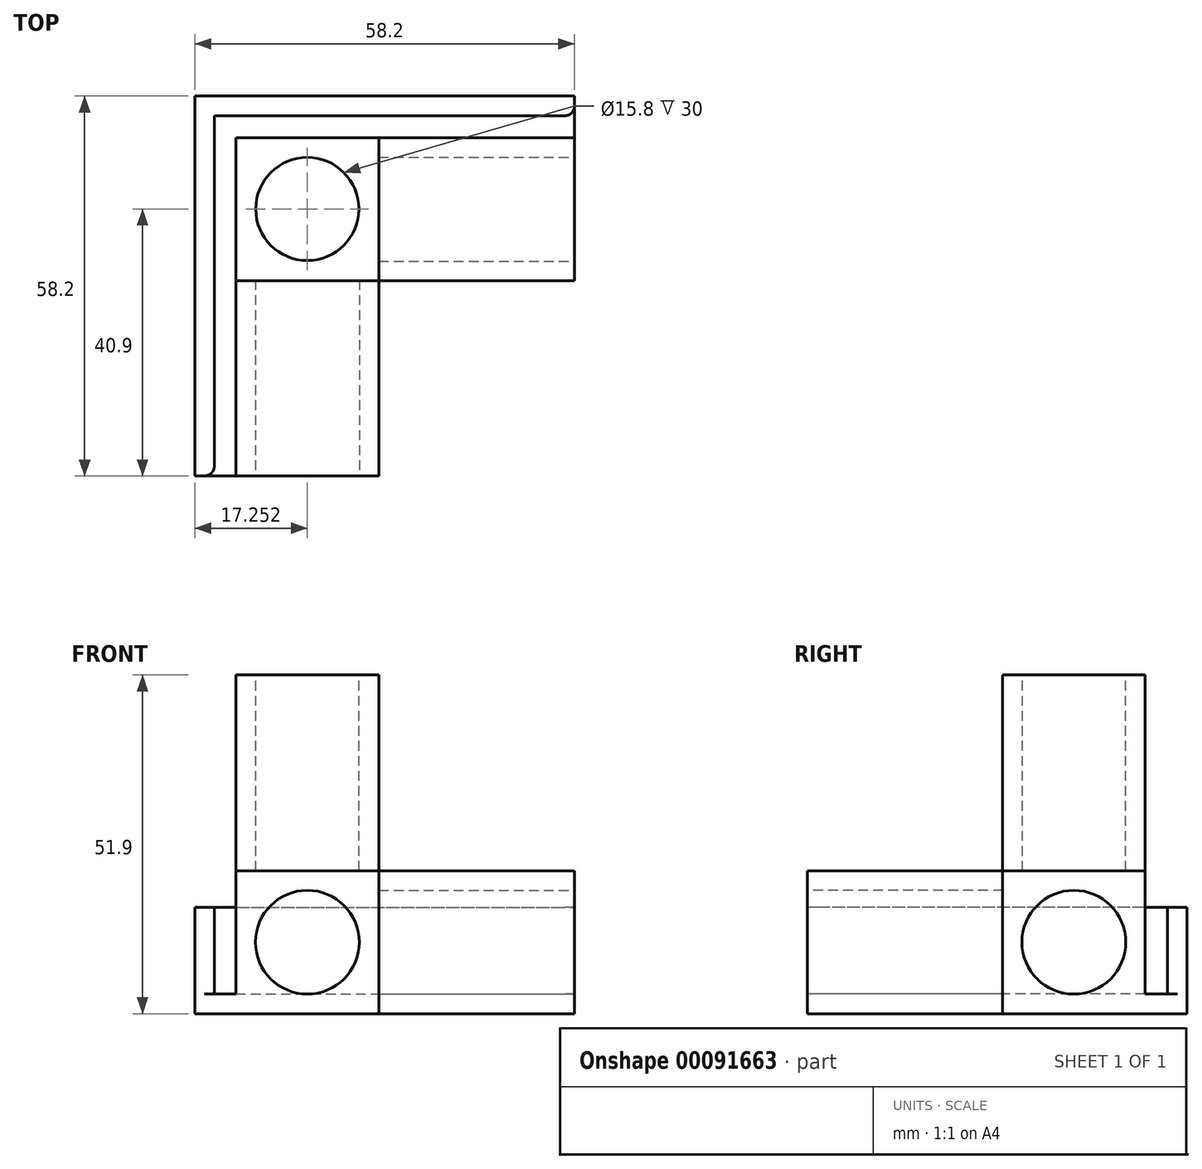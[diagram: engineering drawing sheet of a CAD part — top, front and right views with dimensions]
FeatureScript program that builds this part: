
annotation { "Feature Type Name" : "Feature", "Feature Type Description" : "" }
export const myFeature = defineFeature(function(context is Context, id is Id, definition is map)
    precondition{}
    {
        {
            var Q0;
            Q0=qCreatedBy(makeId("Front.planeOp"),FACE);
            var sketch = newSketch(context, id + "F0", { "sketchPlane" : qUnion([Q0])});
            skLineSegment(sketch, "E0.bottom", {"start": v(-42.3, 45.9) * mm, "end": v(-26.4, 45.9) * mm});
            skLineSegment(sketch, "E0.top", {"start": v(-42.3, 0) * mm, "end": v(-26.4, 0) * mm});
            skLineSegment(sketch, "E0.left", {"start": v(-42.3, 45.9) * mm, "end": v(-42.3, 0) * mm});
            skLineSegment(sketch, "E0.right", {"start": v(-26.4, 45.9) * mm, "end": v(-26.4, 15.9) * mm});
            skLineSegment(sketch, "E1.top", {"start": v(-42.3, 15.9) * mm, "end": v(-26.4, 15.9) * mm});
            skLineSegment(sketch, "E1.left", {"start": v(-42.3, 0) * mm, "end": v(-42.3, 15.9) * mm});
            skLineSegment(sketch, "E1.right", {"start": v(3.6, 0) * mm, "end": v(3.6, 15.9) * mm});
            skLineSegment(sketch, "E2", {"start": v(-26.4, 15.9) * mm, "end": v(-26.4, 0) * mm});
            skLineSegment(sketch, "E3", {"start": v(-26.4, 15.9) * mm, "end": v(3.6, 15.9) * mm});
            skLineSegment(sketch, "E4", {"start": v(-26.4, 0) * mm, "end": v(-26.4, 0) * mm});
            skLineSegment(sketch, "E5", {"start": v(-42.3, 15.9) * mm, "end": v(-42.3, 15.9) * mm});
            skLineSegment(sketch, "E6", {"start": v(-26.4, 0) * mm, "end": v(3.6, 0) * mm});
            skLineSegment(sketch, "E7.0", {"start": v(-45.3, 48.9) * mm, "end": v(-45.3, -3) * mm});
            skLineSegment(sketch, "E7.1", {"start": v(-45.3, -3) * mm, "end": v(-23.4, -3) * mm});
            skLineSegment(sketch, "E7.2", {"start": v(-23.4, 48.9) * mm, "end": v(-23.4, 18.9) * mm});
            skLineSegment(sketch, "E7.3", {"start": v(-23.4, 18.9) * mm, "end": v(6.6, 18.9) * mm});
            skLineSegment(sketch, "E7.4", {"start": v(6.6, -3) * mm, "end": v(6.6, 18.9) * mm});
            skLineSegment(sketch, "E7.5", {"start": v(-45.3, 48.9) * mm, "end": v(-23.4, 48.9) * mm});
            skLineSegment(sketch, "E7.6", {"start": v(-23.4, -3) * mm, "end": v(6.6, -3) * mm});
            skPoint(sketch, "E8", {"position": v(-34.36, 7.95) * mm});
            skPoint(sketch, "E8.positionSnap0", {"position": v(-26.4, 7.95) * mm});
            skPoint(sketch, "E8.positionSnap1", {"position": v(-34.36, 15.9) * mm});
            skCircle(sketch, "E9", {"center": v(-34.36, 7.95) * mm, "radius": 7.95 * mm});
            skLineSegment(sketch, "E10", {"start": v(-23.4, 18.9) * mm, "end": v(-45.3, 18.9) * mm});
            skLineSegment(sketch, "E11", {"start": v(-23.4, 18.9) * mm, "end": v(-23.4, -3) * mm});
            skSolve(sketch);
        }
        {
            var Q0;
            {var subQ1=sQuery(id+"F0.wireOp",EDGE,"E1.top");var subQ3=sQuery(id+"F0.wireOp",EDGE,"E9");var subQ4=makeQuery(id+"F0.imprint","INTERSECT",VERTEX,{"derivedFrom":[subQ1,subQ3]});Q0=makeQuery(id+"F0.imprint","IMPRINT",FACE,{"disambiguationData":[TD([[makeQuery(id+"F0.imprint","IMPRINT",EDGE,{"disambiguationData":[TD([[subQ4,-1.0]])],"derivedFrom":subQ3}),-1.0]])]});}
            var Q1;
            {var subQ0=sQuery(id+"F0.wireOp",EDGE,"E9");var subQ1=makeQuery(id+"F0.imprint","INTERSECT",VERTEX,{"derivedFrom":[sQuery(id+"F0.wireOp",EDGE,"E1.top"),subQ0]});Q1=makeQuery(id+"F0.imprint","IMPRINT",FACE,{"disambiguationData":[TD([[makeQuery(id+"F0.imprint","IMPRINT",EDGE,{"disambiguationData":[TD([[subQ1,1.0]])],"derivedFrom":subQ0}),1.0]])]});}
            var Q2;
            {var subQ5=sQuery(id+"F0.wireOp",EDGE,"E0.bottom");Q2=makeQuery(id+"F0.imprint","IMPRINT",FACE,{"disambiguationData":[TD([[makeQuery(id+"F0.imprint","IMPRINT",EDGE,{"derivedFrom":subQ5}),1.0]])]});}
            var Q3;
            {var subQ0=sQuery(id+"F0.wireOp",EDGE,"E1.right");Q3=makeQuery(id+"F0.imprint","IMPRINT",FACE,{"disambiguationData":[TD([[makeQuery(id+"F0.imprint","IMPRINT",EDGE,{"derivedFrom":subQ0}),1.0]])]});}
            var Q4;
            {var subQ0=sQuery(id+"F0.wireOp",EDGE,"E0.bottom");Q4=makeQuery(id+"F0.imprint","IMPRINT",FACE,{"disambiguationData":[TD([[makeQuery(id+"F0.imprint","IMPRINT",EDGE,{"derivedFrom":subQ0}),-1.0]])]});}
            var Q5;
            {var subQ0=sQuery(id+"F0.wireOp",EDGE,"E1.left");var subQ1=sQuery(id+"F0.wireOp",EDGE,"E0.top");var subQ2=makeQuery(id+"F0.imprint","INTERSECT",VERTEX,{"derivedFrom":[subQ1,subQ0]});Q5=makeQuery(id+"F0.imprint","IMPRINT",FACE,{"disambiguationData":[TD([[makeQuery(id+"F0.imprint","IMPRINT",EDGE,{"disambiguationData":[TD([[subQ2,-1.0]])],"derivedFrom":subQ1}),1.0]])]});}
            var Q6;
            {var subQ1=sQuery(id+"F0.wireOp",EDGE,"E0.top");var subQ3=sQuery(id+"F0.wireOp",EDGE,"E9");var subQ4=makeQuery(id+"F0.imprint","INTERSECT",VERTEX,{"derivedFrom":[subQ1,subQ3]});Q6=makeQuery(id+"F0.imprint","IMPRINT",FACE,{"disambiguationData":[TD([[makeQuery(id+"F0.imprint","IMPRINT",EDGE,{"disambiguationData":[TD([[subQ4,-1.0]])],"derivedFrom":subQ3}),-1.0]])]});}
            var Q7;
            {var subQ1=sQuery(id+"F0.wireOp",EDGE,"E1.top");var subQ3=sQuery(id+"F0.wireOp",EDGE,"E9");var subQ4=makeQuery(id+"F0.imprint","INTERSECT",VERTEX,{"derivedFrom":[subQ1,subQ3]});Q7=makeQuery(id+"F0.imprint","IMPRINT",FACE,{"disambiguationData":[TD([[makeQuery(id+"F0.imprint","IMPRINT",EDGE,{"disambiguationData":[TD([[subQ4,1.0]])],"derivedFrom":subQ3}),-1.0]])]});}
            var Q8;
            {var subQ5=sQuery(id+"F0.wireOp",EDGE,"E1.right");Q8=makeQuery(id+"F0.imprint","IMPRINT",FACE,{"disambiguationData":[TD([[makeQuery(id+"F0.imprint","IMPRINT",EDGE,{"derivedFrom":subQ5}),-1.0]])]});}
            var Q9;
            {var subQ4=sQuery(id+"F0.wireOp",EDGE,"E0.left");var subQ6=sQuery(id+"F0.wireOp",EDGE,"E10");var subQ8=makeQuery(id+"F0.imprint","INTERSECT",VERTEX,{"derivedFrom":[subQ4,subQ6]});Q9=makeQuery(id+"F0.imprint","IMPRINT",FACE,{"disambiguationData":[TD([[makeQuery(id+"F0.imprint","IMPRINT",EDGE,{"disambiguationData":[TD([[subQ8,1.0]])],"derivedFrom":subQ6}),1.0]])]});}
            var Q10;
            {var subQ3=sQuery(id+"F0.wireOp",EDGE,"E11");var subQ5=sQuery(id+"F0.wireOp",EDGE,"E3");var subQ8=makeQuery(id+"F0.imprint","INTERSECT",VERTEX,{"derivedFrom":[subQ5,subQ3]});Q10=makeQuery(id+"F0.imprint","IMPRINT",FACE,{"disambiguationData":[TD([[makeQuery(id+"F0.imprint","IMPRINT",EDGE,{"disambiguationData":[TD([[subQ8,-1.0]])],"derivedFrom":subQ3}),-1.0]])]});}
            var Q11;
            {var subQ14=sQuery(id+"F0.wireOp",EDGE,"E7.1");Q11=makeQuery(id+"F0.imprint","IMPRINT",FACE,{"disambiguationData":[TD([[makeQuery(id+"F0.imprint","IMPRINT",EDGE,{"derivedFrom":subQ14}),1.0]])]});}
            var Q12;
            {var subQ1=sQuery(id+"F0.wireOp",EDGE,"E0.right");var subQ3=sQuery(id+"F0.wireOp",EDGE,"E10");var subQ4=makeQuery(id+"F0.imprint","INTERSECT",VERTEX,{"derivedFrom":[subQ1,subQ3]});Q12=makeQuery(id+"F0.imprint","IMPRINT",FACE,{"disambiguationData":[TD([[makeQuery(id+"F0.imprint","IMPRINT",EDGE,{"disambiguationData":[TD([[subQ4,-1.0]])],"derivedFrom":subQ1}),1.0]])]});}
            extrude(context, id + "F1", {"entities" : qUnion([Q0, Q1, Q2, Q3, Q4, Q5, Q6, Q7, Q8, Q9, Q10, Q11, Q12]), "depth" : (15.9 + 6) * mm});
        }
        {
            var Q0;
            {var subQ14=sQuery(id+"F0.wireOp",EDGE,"E7.1");Q0=makeQuery(id+"F0.imprint","IMPRINT",FACE,{"disambiguationData":[TD([[makeQuery(id+"F0.imprint","IMPRINT",EDGE,{"derivedFrom":subQ14}),1.0]])]});}
            var Q1;
            {var subQ0=sQuery(id+"F0.wireOp",EDGE,"E9");var subQ1=makeQuery(id+"F0.imprint","INTERSECT",VERTEX,{"derivedFrom":[sQuery(id+"F0.wireOp",EDGE,"E1.top"),subQ0]});Q1=makeQuery(id+"F0.imprint","IMPRINT",FACE,{"disambiguationData":[TD([[makeQuery(id+"F0.imprint","IMPRINT",EDGE,{"disambiguationData":[TD([[subQ1,1.0]])],"derivedFrom":subQ0}),1.0]])]});}
            var Q2;
            {var subQ4=sQuery(id+"F0.wireOp",EDGE,"E0.left");var subQ6=sQuery(id+"F0.wireOp",EDGE,"E10");var subQ8=makeQuery(id+"F0.imprint","INTERSECT",VERTEX,{"derivedFrom":[subQ4,subQ6]});Q2=makeQuery(id+"F0.imprint","IMPRINT",FACE,{"disambiguationData":[TD([[makeQuery(id+"F0.imprint","IMPRINT",EDGE,{"disambiguationData":[TD([[subQ8,1.0]])],"derivedFrom":subQ6}),1.0]])]});}
            var Q3;
            {var subQ3=sQuery(id+"F0.wireOp",EDGE,"E11");var subQ5=sQuery(id+"F0.wireOp",EDGE,"E3");var subQ8=makeQuery(id+"F0.imprint","INTERSECT",VERTEX,{"derivedFrom":[subQ5,subQ3]});Q3=makeQuery(id+"F0.imprint","IMPRINT",FACE,{"disambiguationData":[TD([[makeQuery(id+"F0.imprint","IMPRINT",EDGE,{"disambiguationData":[TD([[subQ8,-1.0]])],"derivedFrom":subQ3}),-1.0]])]});}
            var Q4;
            {var subQ1=sQuery(id+"F0.wireOp",EDGE,"E0.right");var subQ3=sQuery(id+"F0.wireOp",EDGE,"E10");var subQ4=makeQuery(id+"F0.imprint","INTERSECT",VERTEX,{"derivedFrom":[subQ1,subQ3]});Q4=makeQuery(id+"F0.imprint","IMPRINT",FACE,{"disambiguationData":[TD([[makeQuery(id+"F0.imprint","IMPRINT",EDGE,{"disambiguationData":[TD([[subQ4,-1.0]])],"derivedFrom":subQ1}),1.0]])]});}
            var Q5;
            {var subQ1=sQuery(id+"F0.wireOp",EDGE,"E1.top");var subQ3=sQuery(id+"F0.wireOp",EDGE,"E9");var subQ4=makeQuery(id+"F0.imprint","INTERSECT",VERTEX,{"derivedFrom":[subQ1,subQ3]});Q5=makeQuery(id+"F0.imprint","IMPRINT",FACE,{"disambiguationData":[TD([[makeQuery(id+"F0.imprint","IMPRINT",EDGE,{"disambiguationData":[TD([[subQ4,1.0]])],"derivedFrom":subQ3}),-1.0]])]});}
            var Q6;
            {var subQ1=sQuery(id+"F0.wireOp",EDGE,"E1.top");var subQ3=sQuery(id+"F0.wireOp",EDGE,"E9");var subQ4=makeQuery(id+"F0.imprint","INTERSECT",VERTEX,{"derivedFrom":[subQ1,subQ3]});Q6=makeQuery(id+"F0.imprint","IMPRINT",FACE,{"disambiguationData":[TD([[makeQuery(id+"F0.imprint","IMPRINT",EDGE,{"disambiguationData":[TD([[subQ4,-1.0]])],"derivedFrom":subQ3}),-1.0]])]});}
            var Q7;
            {var subQ0=sQuery(id+"F0.wireOp",EDGE,"E1.left");var subQ1=sQuery(id+"F0.wireOp",EDGE,"E0.top");var subQ2=makeQuery(id+"F0.imprint","INTERSECT",VERTEX,{"derivedFrom":[subQ1,subQ0]});Q7=makeQuery(id+"F0.imprint","IMPRINT",FACE,{"disambiguationData":[TD([[makeQuery(id+"F0.imprint","IMPRINT",EDGE,{"disambiguationData":[TD([[subQ2,-1.0]])],"derivedFrom":subQ1}),1.0]])]});}
            var Q8;
            {var subQ1=sQuery(id+"F0.wireOp",EDGE,"E0.top");var subQ3=sQuery(id+"F0.wireOp",EDGE,"E9");var subQ4=makeQuery(id+"F0.imprint","INTERSECT",VERTEX,{"derivedFrom":[subQ1,subQ3]});Q8=makeQuery(id+"F0.imprint","IMPRINT",FACE,{"disambiguationData":[TD([[makeQuery(id+"F0.imprint","IMPRINT",EDGE,{"disambiguationData":[TD([[subQ4,-1.0]])],"derivedFrom":subQ3}),-1.0]])]});}
            extrude(context, id + "F2", {"entities" : qUnion([Q0, Q1, Q2, Q3, Q4, Q5, Q6, Q7, Q8]), "operationType" : NewBodyOperationType.ADD, "depth" : (15.8 + 6 + 30) * mm});
        }
        {
            var Q0;
            Q0=makeQuery(id+"F2.opExtrude","CAP_FACE",FACE,{"disambiguationData":[OSD([sQuery(id+"F0.wireOp",EDGE,"E7.0"),sQuery(id+"F0.wireOp",EDGE,"E7.1"),sQuery(id+"F0.wireOp",EDGE,"E10"),sQuery(id+"F0.wireOp",EDGE,"E11")])],"isStart":false});
            var sketch = newSketch(context, id + "F3", { "sketchPlane" : qUnion([Q0])});
            skCircle(sketch, "E12.0", {"center": v(-34.36, 7.95) * mm, "radius": 7.95 * mm});
            skSolve(sketch);
        }
        {
            var Q0;
            Q0=makeQuery(id+"F1.opExtrude","SWEPT_FACE",FACE,{"disambiguationData":[OSD([sQuery(id+"F0.wireOp",EDGE,"E7.5")])]});
            var sketch = newSketch(context, id + "F4", { "sketchPlane" : qUnion([Q0])});
            skPoint(sketch, "E13", {"position": v(-34.36, -3) * mm});
            skPoint(sketch, "E14", {"position": v(-26.4, -10.9) * mm});
            skPoint(sketch, "E15", {"position": v(-34.36, -10.9) * mm});
            skPoint(sketch, "E16", {"position": v(-62.98, 75) * mm});
            skPoint(sketch, "E17.orphan", {"position": v(-42.3, -3) * mm});
            skPoint(sketch, "E18.orphan", {"position": v(-26.4, -3) * mm});
            skPoint(sketch, "E19.orphan", {"position": v(-26.4, -18.8) * mm});
            skCircle(sketch, "E20", {"center": v(-34.36, -10.9) * mm, "radius": 7.9 * mm});
            skSolve(sketch);
        }
        {
            var Q0;
            Q0=makeQuery(id+"F1.opExtrude","SWEPT_FACE",FACE,{"disambiguationData":[OSD([sQuery(id+"F0.wireOp",EDGE,"E7.4")])]});
            var sketch = newSketch(context, id + "F5", { "sketchPlane" : qUnion([Q0])});
            skLineSegment(sketch, "E21.0", {"start": v(-18.9, 15.9) * mm, "end": v(-3, 15.9) * mm});
            skLineSegment(sketch, "E21.1", {"start": v(-18.9, 0) * mm, "end": v(-18.9, 15.9) * mm});
            skLineSegment(sketch, "E21.2", {"start": v(-18.9, 0) * mm, "end": v(-3, 0) * mm});
            skLineSegment(sketch, "E21.3", {"start": v(-3, 0) * mm, "end": v(-3, 15.9) * mm});
            skCircle(sketch, "E22", {"center": v(-10.95, 7.95) * mm, "radius": 7.95 * mm});
            skPoint(sketch, "E22.centerSnap0", {"position": v(-10.95, 0) * mm});
            skPoint(sketch, "E22.centerSnap1", {"position": v(-3, 7.95) * mm});
            skSolve(sketch);
        }
        {
            var Q0;
            Q0=makeQuery(id+"F3.imprint","IMPRINT",FACE,{"disambiguationData":[TD([[makeQuery(id+"F3.imprint","IMPRINT",EDGE,{"derivedFrom":sQuery(id+"F3.wireOp",EDGE,"E12.0")}),1.0]])]});
            extrude(context, id + "F6", {"entities" : qUnion([Q0]), "operationType" : NewBodyOperationType.REMOVE, "oppositeDirection" : true, "depth" : 30 * mm});
        }
        {
            var Q0;
            {var subQ0=sQuery(id+"F5.wireOp",EDGE,"E22");var subQ1=makeQuery(id+"F5.imprint","INTERSECT",VERTEX,{"derivedFrom":[sQuery(id+"F5.wireOp",EDGE,"E21.1"),subQ0]});Q0=makeQuery(id+"F5.imprint","IMPRINT",FACE,{"disambiguationData":[TD([[makeQuery(id+"F5.imprint","IMPRINT",EDGE,{"disambiguationData":[TD([[subQ1,1.0]])],"derivedFrom":subQ0}),1.0]])]});}
            extrude(context, id + "F7", {"entities" : qUnion([Q0]), "operationType" : NewBodyOperationType.REMOVE, "oppositeDirection" : true, "depth" : 30 * mm});
        }
        {
            var Q0;
            Q0=makeQuery(id+"F4.imprint","IMPRINT",FACE,{"disambiguationData":[TD([[makeQuery(id+"F4.imprint","IMPRINT",EDGE,{"derivedFrom":sQuery(id+"F4.wireOp",EDGE,"E20")}),1.0]])]});
            var Q1;
            Q1=sQuery(id+"F4.wireOp",EDGE,"E20");
            extrude(context, id + "F8", {"entities" : qUnion([Q0]), "operationType" : NewBodyOperationType.REMOVE, "surfaceEntities" : qUnion([Q1]), "oppositeDirection" : true, "depth" : 30 * mm});
        }
        {
            var Q0;
            Q0=makeQuery(id+"F2.opExtrude","CAP_FACE",FACE,{"disambiguationData":[OSD([sQuery(id+"F0.wireOp",EDGE,"E7.0"),sQuery(id+"F0.wireOp",EDGE,"E7.1"),sQuery(id+"F0.wireOp",EDGE,"E10"),sQuery(id+"F0.wireOp",EDGE,"E11")])],"isStart":false});
            var sketch = newSketch(context, id + "F9", { "sketchPlane" : qUnion([Q0])});
            skLineSegment(sketch, "E23", {"start": v(-45.3, -3) * mm, "end": v(-51.6, -3) * mm});
            skLineSegment(sketch, "E24", {"start": v(-51.6, -3) * mm, "end": v(-51.6, 13.3) * mm});
            skLineSegment(sketch, "E25", {"start": v(-51.6, 13.3) * mm, "end": v(-48.6, 13.3) * mm});
            skLineSegment(sketch, "E26", {"start": v(-48.6, 13.3) * mm, "end": v(-48.6, 0) * mm});
            skLineSegment(sketch, "E27", {"start": v(-48.6, 0) * mm, "end": v(-45.3, 0) * mm});
            skSolve(sketch);
        }
        {
            var Q0;
            {var subQ0=sQuery(id+"F9.wireOp",EDGE,"E23");Q0=makeQuery(id+"F9.imprint","IMPRINT",FACE,{"disambiguationData":[TD([[makeQuery(id+"F9.imprint","IMPRINT",EDGE,{"derivedFrom":subQ0}),-1.0]])]});}
            extrude(context, id + "F10", {"entities" : qUnion([Q0]), "operationType" : NewBodyOperationType.ADD, "oppositeDirection" : true, "depth" : (6 + 15.9 + 30 + 6.3) * mm});
        }
        {
            var Q0;
            Q0=makeQuery(id+"F1.opExtrude","SWEPT_FACE",FACE,{"disambiguationData":[OSD([sQuery(id+"F0.wireOp",EDGE,"E7.4")])]});
            var sketch = newSketch(context, id + "F11", { "sketchPlane" : qUnion([Q0])});
            skLineSegment(sketch, "E28.0.0", {"start": v(6.4, 0) * mm, "end": v(0, 0) * mm});
            skLineSegment(sketch, "E28.0.1", {"start": v(0, 0) * mm, "end": v(0, -3) * mm});
            skLineSegment(sketch, "E28.0.2", {"start": v(0, -3) * mm, "end": v(6.4, -3) * mm});
            skLineSegment(sketch, "E28.0.3", {"start": v(6.4, -3) * mm, "end": v(6.4, 0) * mm});
            skLineSegment(sketch, "E29.0", {"start": v(6.4, 13.3) * mm, "end": v(6.4, 0) * mm});
            skLineSegment(sketch, "E30", {"start": v(6.4, 13.3) * mm, "end": v(3.4, 13.3) * mm});
            skLineSegment(sketch, "E31", {"start": v(3.4, 13.3) * mm, "end": v(3.4, 0) * mm});
            skSolve(sketch);
        }
        {
            var Q0;
            Q0 = qSketchRegion(id + "F11", true);
            extrude(context, id + "F12", {"entities" : qUnion([Q0]), "operationType" : NewBodyOperationType.ADD, "endBound" : BoundingType.UP_TO_NEXT, "oppositeDirection" : true, "depth" : 25 * mm});
        }
        {
            var Q0;
            Q0=makeQuery(id+"F12.opExtrude","CAP_EDGE",EDGE,{"disambiguationData":[OSD([sQuery(id+"F11.wireOp",EDGE,"E31")])],"isStart":true});
            var Q1;
            Q1=makeQuery(id+"F10.opExtrude","CAP_EDGE",EDGE,{"disambiguationData":[OSD([sQuery(id+"F9.wireOp",EDGE,"E26")])],"isStart":true});
            fillet(context, id + "F13", {"entities" : qUnion([Q0, Q1]), "radius" : 1.5 * mm, "tangentPropagation" : true, "allowEdgeOverflow" : false});
        }
    });
